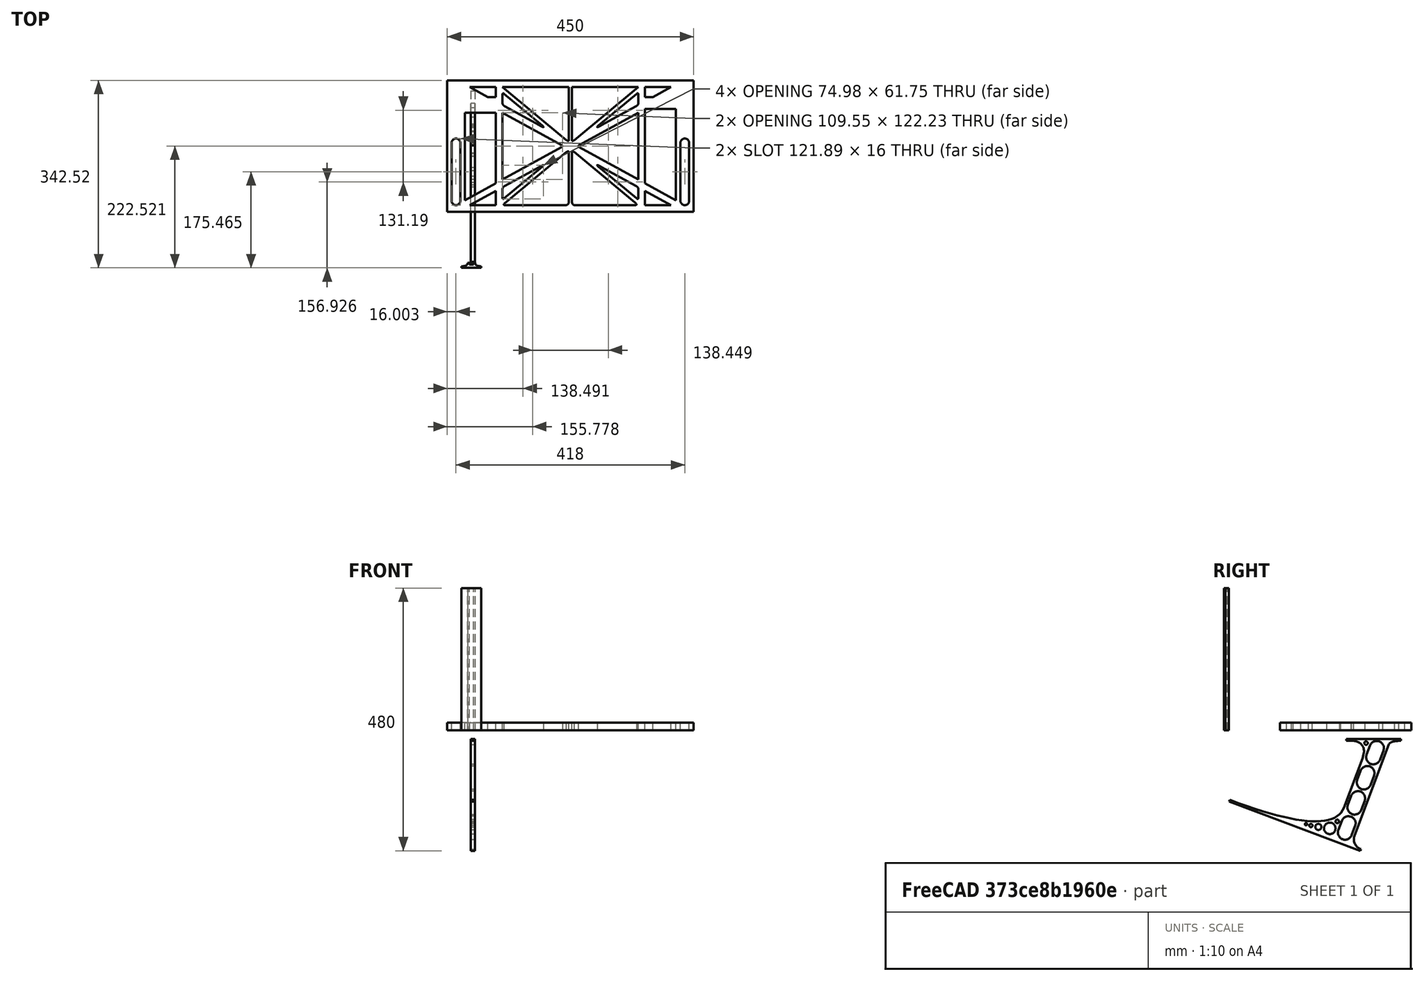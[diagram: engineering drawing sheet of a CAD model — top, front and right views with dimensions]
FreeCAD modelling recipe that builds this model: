
FCSTD DOCUMENT  (FreeCAD 0.19R0.19.2)
Label: laptopStand083
License: All rights reserved
LicenseURL: http://en.wikipedia.org/wiki/All_rights_reserved
objects: Sketcher::SketchObject×3, Part::Extrusion×3
note: 6 computed .brp shape members not serialized (recipe doc carries the construction recipe); baked Part::Feature solids carry a one-line shape summary decoded from their .brp

FEATURE [Sketcher::SketchObject] Sketch
  FullyConstrained = true
  sketch-geometry (202):
    g0: LineSegment StartX=-10.9272 StartY=-82.7794 StartZ=0 EndX=46.0728 EndY=-51.4823 EndZ=0
    g1: LineSegment StartX=366.073 StartY=-91.7794 StartZ=0 EndX=318.073 EndY=-65.424 EndZ=0
    g2: LineSegment StartX=-10.9272 StartY=77.3346 StartZ=0 EndX=-10.9272 EndY=-82.7794 EndZ=0
    g3: LineSegment StartX=375.073 StartY=-82.7794 StartZ=0 EndX=375.073 EndY=83.9235 EndZ=0
    g4: LineSegment StartX=-1.92719 StartY=-91.7794 StartZ=0 EndX=46.0728 EndY=-91.7794 EndZ=0
    g5: LineSegment StartX=318.073 StartY=124.221 StartZ=0 EndX=366.073 EndY=124.221 EndZ=0
    g6: LineSegment StartX=306.073 StartY=124.221 StartZ=0 EndX=189.124 EndY=27.0628 EndZ=0
    g7: LineSegment StartX=175.022 StartY=27.0628 StartZ=0 EndX=58.0728 EndY=124.221 EndZ=0
    g8: LineSegment StartX=306.073 StartY=77.3346 StartZ=0 EndX=306.073 EndY=-44.8935 EndZ=0
    g9: LineSegment StartX=318.073 StartY=83.9235 StartZ=0 EndX=318.073 EndY=-51.4823 EndZ=0
    g10: LineSegment StartX=318.073 StartY=-51.4823 StartZ=0 EndX=375.073 EndY=-82.7794 EndZ=0
    g11: LineSegment StartX=318.073 StartY=-65.424 StartZ=0 EndX=318.073 EndY=-91.7794 EndZ=0
    g12: LineSegment StartX=318.073 StartY=-91.7794 StartZ=0 EndX=366.073 EndY=-91.7794 EndZ=0
    g13: LineSegment StartX=58.0728 StartY=-44.8935 StartZ=0 EndX=58.0728 EndY=77.3346 EndZ=0
    g14: LineSegment StartX=46.0728 StartY=-65.424 StartZ=0 EndX=-1.92719 EndY=-91.7794 EndZ=0
    g15: LineSegment StartX=46.0728 StartY=-65.424 StartZ=0 EndX=46.0728 EndY=-91.7794 EndZ=0
    g16: LineSegment StartX=46.0728 StartY=77.3346 StartZ=0 EndX=46.0728 EndY=-51.4823 EndZ=0
    g17: LineSegment StartX=-42.9272 StartY=136.221 StartZ=0 EndX=-42.9272 EndY=-103.779 EndZ=0
    g18: LineSegment StartX=407.073 StartY=136.221 StartZ=0 EndX=407.073 EndY=-103.779 EndZ=0
    g19: LineSegment StartX=179.022 StartY=27.0628 StartZ=0 EndX=179.022 EndY=124.221 EndZ=0
    g20: LineSegment StartX=185.124 StartY=27.0628 StartZ=0 EndX=185.124 EndY=124.221 EndZ=0
    g21: ArcOfCircle CenterX=-26.9272 CenterY=22.1087 CenterZ=0 NormalX=0 NormalY=0 NormalZ=1 AngleXU=0 Radius=8 StartAngle=1e-16 EndAngle=3.14159
    g22: ArcOfCircle CenterX=-26.9272 CenterY=-83.7794 CenterZ=0 NormalX=0 NormalY=0 NormalZ=1 AngleXU=0 Radius=8 StartAngle=3.14159 EndAngle=6.28319
    g23: LineSegment StartX=-34.9272 StartY=22.1087 StartZ=0 EndX=-34.9272 EndY=-83.7794 EndZ=0
    g24: LineSegment StartX=-18.9272 StartY=22.1087 StartZ=0 EndX=-18.9272 EndY=-83.7794 EndZ=0
    g25: ArcOfCircle CenterX=391.073 CenterY=22.1087 CenterZ=0 NormalX=0 NormalY=0 NormalZ=1 AngleXU=0 Radius=8 StartAngle=-4.4e-15 EndAngle=3.14159
    g26: LineSegment StartX=399.073 StartY=22.1087 StartZ=0 EndX=399.073 EndY=-83.7794 EndZ=0
    g27: LineSegment StartX=383.073 StartY=22.1087 StartZ=0 EndX=383.073 EndY=-83.7794 EndZ=0
    g28: ArcOfCircle CenterX=391.073 CenterY=-83.7794 CenterZ=0 NormalX=0 NormalY=0 NormalZ=1 AngleXU=0 Radius=8 StartAngle=3.14159 EndAngle=6.28319
    g29: Circle CenterX=175.022 CenterY=27.0628 CenterZ=0 NormalX=0 NormalY=0 NormalZ=1 AngleXU=0 Radius=1
    g30: Circle CenterX=179.022 CenterY=24.8665 CenterZ=0 NormalX=0 NormalY=0 NormalZ=1 AngleXU=0 Radius=1
    g31: Circle CenterX=179.022 CenterY=27.0628 CenterZ=0 NormalX=0 NormalY=0 NormalZ=1 AngleXU=0 Radius=1
    g32: BSplineCurve PolesCount=3 KnotsCount=2 Degree=2 IsPeriodic=0
    g33: GeomPoint X=175.022 Y=27.0628 Z=0
    g34: GeomPoint X=179.022 Y=27.0628 Z=0
    g35: Circle CenterX=189.124 CenterY=27.0628 CenterZ=0 NormalX=0 NormalY=0 NormalZ=1 AngleXU=0 Radius=1
    g36: Circle CenterX=185.124 CenterY=24.8665 CenterZ=0 NormalX=0 NormalY=0 NormalZ=1 AngleXU=0 Radius=1
    g37: Circle CenterX=185.124 CenterY=27.0628 CenterZ=0 NormalX=0 NormalY=0 NormalZ=1 AngleXU=0 Radius=1
    g38: BSplineCurve PolesCount=3 KnotsCount=2 Degree=2 IsPeriodic=0
    g39: GeomPoint X=189.124 Y=27.0628 Z=0
    g40: GeomPoint X=185.124 Y=27.0628 Z=0
    g41: Circle CenterX=175.022 CenterY=5.37834 CenterZ=0 NormalX=0 NormalY=0 NormalZ=1 AngleXU=0 Radius=1
    g42: Circle CenterX=179.022 CenterY=7.57463 CenterZ=0 NormalX=0 NormalY=0 NormalZ=1 AngleXU=0 Radius=1
    g43: Circle CenterX=179.022 CenterY=5.34704 CenterZ=0 NormalX=0 NormalY=0 NormalZ=1 AngleXU=0 Radius=1
    g44: BSplineCurve PolesCount=3 KnotsCount=2 Degree=2 IsPeriodic=0
    g45: GeomPoint X=175.022 Y=5.37834 Z=0
    g46: GeomPoint X=179.022 Y=5.34704 Z=0
    g47: Circle CenterX=189.124 CenterY=5.37834 CenterZ=0 NormalX=0 NormalY=0 NormalZ=1 AngleXU=0 Radius=1
    g48: Circle CenterX=185.124 CenterY=7.57463 CenterZ=0 NormalX=0 NormalY=0 NormalZ=1 AngleXU=0 Radius=1
    g49: Circle CenterX=185.124 CenterY=5.34704 CenterZ=0 NormalX=0 NormalY=0 NormalZ=1 AngleXU=0 Radius=1
    g50: BSplineCurve PolesCount=3 KnotsCount=2 Degree=2 IsPeriodic=0
    g51: GeomPoint X=189.124 Y=5.37834 Z=0
    g52: GeomPoint X=185.124 Y=5.34704 Z=0
    g53: Circle CenterX=165.871 CenterY=18.1458 CenterZ=0 NormalX=0 NormalY=0 NormalZ=1 AngleXU=0 Radius=1
    g54: Circle CenterX=169.377 CenterY=16.2206 CenterZ=0 NormalX=0 NormalY=0 NormalZ=1 AngleXU=0 Radius=1
    g55: Circle CenterX=165.871 CenterY=14.2954 CenterZ=0 NormalX=0 NormalY=0 NormalZ=1 AngleXU=0 Radius=1
    g56: BSplineCurve PolesCount=3 KnotsCount=2 Degree=2 IsPeriodic=0
    g57: GeomPoint X=165.871 Y=18.1458 Z=0
    g58: GeomPoint X=165.871 Y=14.2954 Z=0
    g59: Circle CenterX=198.275 CenterY=18.1458 CenterZ=0 NormalX=0 NormalY=0 NormalZ=1 AngleXU=0 Radius=1
    g60: Circle CenterX=194.768 CenterY=16.2206 CenterZ=0 NormalX=0 NormalY=0 NormalZ=1 AngleXU=0 Radius=1
    g61: Circle CenterX=198.275 CenterY=14.2954 CenterZ=0 NormalX=0 NormalY=0 NormalZ=1 AngleXU=0 Radius=1
    g62: BSplineCurve PolesCount=3 KnotsCount=2 Degree=2 IsPeriodic=0
    g63: GeomPoint X=198.275 Y=18.1458 Z=0
    g64: GeomPoint X=198.275 Y=14.2954 Z=0
    g65: LineSegment StartX=165.871 StartY=18.1458 StartZ=0 EndX=58.0728 EndY=77.3346 EndZ=0
    g66: LineSegment StartX=58.0728 StartY=-44.8935 StartZ=0 EndX=165.871 EndY=14.2954 EndZ=0
    g67: LineSegment StartX=198.275 StartY=18.1458 StartZ=0 EndX=306.073 EndY=77.3346 EndZ=0
    g68: LineSegment StartX=198.275 StartY=14.2954 StartZ=0 EndX=306.073 EndY=-44.8935 EndZ=0
    g69: LineSegment StartX=407.073 StartY=-103.779 StartZ=0 EndX=-42.9272 EndY=-103.779 EndZ=0
    g70: LineSegment StartX=407.073 StartY=136.221 StartZ=0 EndX=-42.9272 EndY=136.221 EndZ=0
    g71: LineSegment StartX=46.0728 StartY=77.3346 StartZ=0 EndX=-10.9272 EndY=77.3346 EndZ=0
    g72: LineSegment StartX=46.0728 StartY=105.865 StartZ=0 EndX=31.5028 EndY=105.865 EndZ=0
    g73: LineSegment StartX=46.0728 StartY=124.221 StartZ=0 EndX=46.0728 EndY=105.865 EndZ=0
    g74: LineSegment StartX=-1.92719 StartY=124.221 StartZ=0 EndX=31.5028 EndY=105.865 EndZ=0
    g75: LineSegment StartX=46.0728 StartY=124.221 StartZ=0 EndX=-1.92719 EndY=124.221 EndZ=0
    g76: LineSegment StartX=318.073 StartY=83.9235 StartZ=0 EndX=375.073 EndY=83.9235 EndZ=0
    g77: LineSegment StartX=318.073 StartY=105.865 StartZ=0 EndX=332.643 EndY=105.865 EndZ=0
    g78: LineSegment StartX=332.643 StartY=105.865 StartZ=0 EndX=366.073 EndY=124.221 EndZ=0
    g79: LineSegment StartX=318.073 StartY=124.221 StartZ=0 EndX=318.073 EndY=105.865 EndZ=0
    g80: Circle CenterX=125.607 CenterY=54.1951 CenterZ=0 NormalX=0 NormalY=0 NormalZ=1 AngleXU=0 Radius=1
    g81: Circle CenterX=139.632 CenterY=46.4944 CenterZ=0 NormalX=0 NormalY=0 NormalZ=1 AngleXU=0 Radius=1
    g82: Circle CenterX=127.326 CenterY=56.7187 CenterZ=0 NormalX=0 NormalY=0 NormalZ=1 AngleXU=0 Radius=1
    g83: BSplineCurve PolesCount=3 KnotsCount=2 Degree=2 IsPeriodic=0
    g84: GeomPoint X=125.607 Y=54.1951 Z=0
    g85: GeomPoint X=127.326 Y=56.7187 Z=0
    g86: Circle CenterX=236.821 CenterY=56.7187 CenterZ=0 NormalX=0 NormalY=0 NormalZ=1 AngleXU=0 Radius=1
    g87: Circle CenterX=224.513 CenterY=46.4944 CenterZ=0 NormalX=0 NormalY=0 NormalZ=1 AngleXU=0 Radius=1
    g88: Circle CenterX=238.538 CenterY=54.1951 CenterZ=0 NormalX=0 NormalY=0 NormalZ=1 AngleXU=0 Radius=1
    g89: BSplineCurve PolesCount=3 KnotsCount=2 Degree=2 IsPeriodic=0
    g90: GeomPoint X=236.821 Y=56.7187 Z=0
    g91: GeomPoint X=238.538 Y=54.1951 Z=0
    g92: Circle CenterX=238.538 CenterY=-21.7539 CenterZ=0 NormalX=0 NormalY=0 NormalZ=1 AngleXU=0 Radius=1
    g93: Circle CenterX=224.513 CenterY=-14.0532 CenterZ=0 NormalX=0 NormalY=0 NormalZ=1 AngleXU=0 Radius=1
    g94: Circle CenterX=236.821 CenterY=-24.2775 CenterZ=0 NormalX=0 NormalY=0 NormalZ=1 AngleXU=0 Radius=1
    g95: BSplineCurve PolesCount=3 KnotsCount=2 Degree=2 IsPeriodic=0
    g96: GeomPoint X=238.538 Y=-21.7539 Z=0
    g97: GeomPoint X=236.821 Y=-24.2775 Z=0
    g98: Circle CenterX=125.607 CenterY=-21.7539 CenterZ=0 NormalX=0 NormalY=0 NormalZ=1 AngleXU=0 Radius=1
    g99: Circle CenterX=139.632 CenterY=-14.0532 CenterZ=0 NormalX=0 NormalY=0 NormalZ=1 AngleXU=0 Radius=1
    g100: Circle CenterX=127.325 CenterY=-24.2775 CenterZ=0 NormalX=0 NormalY=0 NormalZ=1 AngleXU=0 Radius=1
    g101: BSplineCurve PolesCount=3 KnotsCount=2 Degree=2 IsPeriodic=0
    g102: GeomPoint X=125.607 Y=-21.7539 Z=0
    g103: GeomPoint X=127.325 Y=-24.2775 Z=0
    g104: Circle CenterX=302.996 CenterY=111.695 CenterZ=0 NormalX=0 NormalY=0 NormalZ=1 AngleXU=0 Radius=1
    g105: Circle CenterX=306.073 CenterY=114.251 CenterZ=0 NormalX=0 NormalY=0 NormalZ=1 AngleXU=0 Radius=1
    g106: Circle CenterX=306.073 CenterY=110.251 CenterZ=0 NormalX=0 NormalY=0 NormalZ=1 AngleXU=0 Radius=1
    g107: BSplineCurve PolesCount=3 KnotsCount=2 Degree=2 IsPeriodic=0
    g108: GeomPoint X=302.996 Y=111.695 Z=0
    g109: GeomPoint X=306.073 Y=110.251 Z=0
    g110: Circle CenterX=306.073 CenterY=95.2763 CenterZ=0 NormalX=0 NormalY=0 NormalZ=1 AngleXU=0 Radius=1
    g111: Circle CenterX=306.073 CenterY=91.2763 CenterZ=0 NormalX=0 NormalY=0 NormalZ=1 AngleXU=0 Radius=1
    g112: Circle CenterX=302.567 CenterY=89.3511 CenterZ=0 NormalX=0 NormalY=0 NormalZ=1 AngleXU=0 Radius=1
    g113: BSplineCurve PolesCount=3 KnotsCount=2 Degree=2 IsPeriodic=0
    g114: GeomPoint X=306.073 Y=95.2763 Z=0
    g115: GeomPoint X=302.567 Y=89.3511 Z=0
    g116: LineSegment StartX=306.073 StartY=110.251 StartZ=0 EndX=306.073 EndY=95.2763 EndZ=0
    g117: LineSegment StartX=302.996 StartY=111.695 StartZ=0 EndX=236.821 EndY=56.7187 EndZ=0
    g118: LineSegment StartX=238.538 StartY=54.1951 StartZ=0 EndX=302.567 EndY=89.3511 EndZ=0
    g119: Circle CenterX=61.1496 CenterY=111.695 CenterZ=0 NormalX=0 NormalY=0 NormalZ=1 AngleXU=0 Radius=1
    g120: Circle CenterX=58.0728 CenterY=114.251 CenterZ=0 NormalX=0 NormalY=0 NormalZ=1 AngleXU=0 Radius=1
    g121: Circle CenterX=58.0728 CenterY=110.251 CenterZ=0 NormalX=0 NormalY=0 NormalZ=1 AngleXU=0 Radius=1
    g122: BSplineCurve PolesCount=3 KnotsCount=2 Degree=2 IsPeriodic=0
    g123: GeomPoint X=61.1496 Y=111.695 Z=0
    g124: GeomPoint X=58.0728 Y=110.251 Z=0
    g125: Circle CenterX=61.5791 CenterY=89.3511 CenterZ=0 NormalX=0 NormalY=0 NormalZ=1 AngleXU=0 Radius=1
    g126: Circle CenterX=58.0728 CenterY=91.2763 CenterZ=0 NormalX=0 NormalY=0 NormalZ=1 AngleXU=0 Radius=1
    g127: Circle CenterX=58.0728 CenterY=95.2763 CenterZ=0 NormalX=0 NormalY=0 NormalZ=1 AngleXU=0 Radius=1
    g128: BSplineCurve PolesCount=3 KnotsCount=2 Degree=2 IsPeriodic=0
    g129: GeomPoint X=61.5791 Y=89.3511 Z=0
    g130: GeomPoint X=58.0728 Y=95.2763 Z=0
    g131: LineSegment StartX=58.0728 StartY=110.251 StartZ=0 EndX=58.0728 EndY=95.2763 EndZ=0
    g132: LineSegment StartX=61.1496 StartY=111.695 StartZ=0 EndX=127.326 EndY=56.7187 EndZ=0
    g133: LineSegment StartX=125.607 StartY=54.1951 StartZ=0 EndX=61.5791 EndY=89.3511 EndZ=0
    g134: Circle CenterX=61.5791 CenterY=-56.9099 CenterZ=0 NormalX=0 NormalY=0 NormalZ=1 AngleXU=0 Radius=1
    g135: Circle CenterX=58.0728 CenterY=-58.8351 CenterZ=0 NormalX=0 NormalY=0 NormalZ=1 AngleXU=0 Radius=1
    g136: Circle CenterX=58.0728 CenterY=-62.8351 CenterZ=0 NormalX=0 NormalY=0 NormalZ=1 AngleXU=0 Radius=1
    g137: BSplineCurve PolesCount=3 KnotsCount=2 Degree=2 IsPeriodic=0
    g138: GeomPoint X=61.5791 Y=-56.9099 Z=0
    g139: GeomPoint X=58.0728 Y=-62.8351 Z=0
    g140: Circle CenterX=58.0728 CenterY=-77.8102 CenterZ=0 NormalX=0 NormalY=0 NormalZ=1 AngleXU=0 Radius=1
    g141: Circle CenterX=58.0728 CenterY=-81.8102 CenterZ=0 NormalX=0 NormalY=0 NormalZ=1 AngleXU=0 Radius=1
    g142: Circle CenterX=61.1496 CenterY=-79.2541 CenterZ=0 NormalX=0 NormalY=0 NormalZ=1 AngleXU=0 Radius=1
    g143: BSplineCurve PolesCount=3 KnotsCount=2 Degree=2 IsPeriodic=0
    g144: GeomPoint X=58.0728 Y=-77.8102 Z=0
    g145: GeomPoint X=61.1496 Y=-79.2541 Z=0
    g146: LineSegment StartX=58.0728 StartY=-62.8351 StartZ=0 EndX=58.0728 EndY=-77.8102 EndZ=0
    g147: LineSegment StartX=61.1496 StartY=-79.2541 StartZ=0 EndX=127.325 EndY=-24.2775 EndZ=0
    g148: LineSegment StartX=125.607 StartY=-21.7539 StartZ=0 EndX=61.5791 EndY=-56.9099 EndZ=0
    g149: Circle CenterX=302.567 CenterY=-56.9099 CenterZ=0 NormalX=0 NormalY=0 NormalZ=1 AngleXU=0 Radius=1
    g150: Circle CenterX=306.073 CenterY=-58.8351 CenterZ=0 NormalX=0 NormalY=0 NormalZ=1 AngleXU=0 Radius=1
    g151: Circle CenterX=306.073 CenterY=-62.8351 CenterZ=0 NormalX=0 NormalY=0 NormalZ=1 AngleXU=0 Radius=1
    g152: BSplineCurve PolesCount=3 KnotsCount=2 Degree=2 IsPeriodic=0
    g153: GeomPoint X=302.567 Y=-56.9099 Z=0
    g154: GeomPoint X=306.073 Y=-62.8351 Z=0
    g155: Circle CenterX=302.996 CenterY=-79.2541 CenterZ=0 NormalX=0 NormalY=0 NormalZ=1 AngleXU=0 Radius=1
    g156: Circle CenterX=306.073 CenterY=-81.8102 CenterZ=0 NormalX=0 NormalY=0 NormalZ=1 AngleXU=0 Radius=1
    g157: Circle CenterX=306.073 CenterY=-77.8102 CenterZ=0 NormalX=0 NormalY=0 NormalZ=1 AngleXU=0 Radius=1
    g158: BSplineCurve PolesCount=3 KnotsCount=2 Degree=2 IsPeriodic=0
    g159: GeomPoint X=302.996 Y=-79.2541 Z=0
    g160: GeomPoint X=306.073 Y=-77.8102 Z=0
    g161: LineSegment StartX=306.073 StartY=-62.8351 StartZ=0 EndX=306.073 EndY=-77.8102 EndZ=0
    g162: LineSegment StartX=302.996 StartY=-79.2541 StartZ=0 EndX=236.821 EndY=-24.2775 EndZ=0
    g163: LineSegment StartX=238.538 StartY=-21.7539 StartZ=0 EndX=302.567 EndY=-56.9099 EndZ=0
    g164: Circle CenterX=61.6457 CenterY=-88.8112 CenterZ=0 NormalX=0 NormalY=0 NormalZ=1 AngleXU=0 Radius=1
    g165: Circle CenterX=58.0728 CenterY=-91.7794 CenterZ=0 NormalX=0 NormalY=0 NormalZ=1 AngleXU=0 Radius=1
    g166: Circle CenterX=63.9135 CenterY=-91.7794 CenterZ=0 NormalX=0 NormalY=0 NormalZ=1 AngleXU=0 Radius=1
    g167: BSplineCurve PolesCount=3 KnotsCount=2 Degree=2 IsPeriodic=0
    g168: GeomPoint X=61.6457 Y=-88.8112 Z=0
    g169: GeomPoint X=63.9135 Y=-91.7794 Z=0
    g170: Circle CenterX=179.022 CenterY=-85.8163 CenterZ=0 NormalX=0 NormalY=0 NormalZ=1 AngleXU=0 Radius=1
    g171: Circle CenterX=179.022 CenterY=-91.7794 CenterZ=0 NormalX=0 NormalY=0 NormalZ=1 AngleXU=0 Radius=1
    g172: Circle CenterX=171.895 CenterY=-91.7794 CenterZ=0 NormalX=0 NormalY=0 NormalZ=1 AngleXU=0 Radius=1
    g173: BSplineCurve PolesCount=3 KnotsCount=2 Degree=2 IsPeriodic=0
    g174: GeomPoint X=179.022 Y=-85.8163 Z=0
    g175: GeomPoint X=171.895 Y=-91.7794 Z=0
    g176: Circle CenterX=185.124 CenterY=-86.2028 CenterZ=0 NormalX=0 NormalY=0 NormalZ=1 AngleXU=0 Radius=1
    g177: Circle CenterX=185.124 CenterY=-91.7794 CenterZ=0 NormalX=0 NormalY=0 NormalZ=1 AngleXU=0 Radius=1
    g178: Circle CenterX=191.747 CenterY=-91.7794 CenterZ=0 NormalX=0 NormalY=0 NormalZ=1 AngleXU=0 Radius=1
    g179: BSplineCurve PolesCount=3 KnotsCount=2 Degree=2 IsPeriodic=0
    g180: GeomPoint X=185.124 Y=-86.2028 Z=0
    g181: GeomPoint X=191.747 Y=-91.7794 Z=0
    g182: Circle CenterX=299.888 CenterY=-86.6413 CenterZ=0 NormalX=0 NormalY=0 NormalZ=1 AngleXU=0 Radius=1
    g183: Circle CenterX=306.073 CenterY=-91.7794 CenterZ=0 NormalX=0 NormalY=0 NormalZ=1 AngleXU=0 Radius=1
    g184: Circle CenterX=298.776 CenterY=-91.7794 CenterZ=0 NormalX=0 NormalY=0 NormalZ=1 AngleXU=0 Radius=1
    g185: BSplineCurve PolesCount=3 KnotsCount=2 Degree=2 IsPeriodic=0
    g186: GeomPoint X=299.888 Y=-86.6413 Z=0
    g187: GeomPoint X=298.776 Y=-91.7794 Z=0
    g188: LineSegment StartX=189.124 StartY=5.37834 StartZ=0 EndX=299.888 EndY=-86.6413 EndZ=0
    g189: LineSegment StartX=298.776 StartY=-91.7794 StartZ=0 EndX=191.747 EndY=-91.7794 EndZ=0
    g190: LineSegment StartX=185.124 StartY=-86.2028 StartZ=0 EndX=185.124 EndY=5.34704 EndZ=0
    g191: LineSegment StartX=179.022 StartY=5.34704 StartZ=0 EndX=179.022 EndY=-85.8163 EndZ=0
    g192: LineSegment StartX=171.895 StartY=-91.7794 StartZ=0 EndX=63.9135 EndY=-91.7794 EndZ=0
    g193: LineSegment StartX=61.6457 StartY=-88.8112 StartZ=0 EndX=175.022 EndY=5.37834 EndZ=0
    g194: LineSegment StartX=306.073 StartY=124.221 StartZ=0 EndX=302.996 EndY=121.665 EndZ=0
    g195: LineSegment StartX=306.073 StartY=124.221 StartZ=0 EndX=302.073 EndY=124.221 EndZ=0
    g196: LineSegment StartX=185.124 StartY=124.221 StartZ=0 EndX=189.124 EndY=124.221 EndZ=0
    g197: LineSegment StartX=185.124 StartY=124.221 StartZ=0 EndX=185.124 EndY=120.221 EndZ=0
    g198: LineSegment StartX=179.022 StartY=124.221 StartZ=0 EndX=179.022 EndY=120.221 EndZ=0
    g199: LineSegment StartX=179.022 StartY=124.221 StartZ=0 EndX=175.022 EndY=124.221 EndZ=0
    g200: LineSegment StartX=58.0728 StartY=124.221 StartZ=0 EndX=62.0728 EndY=124.221 EndZ=0
    g201: LineSegment StartX=58.0728 StartY=124.221 StartZ=0 EndX=61.1496 EndY=121.665 EndZ=0
  constraints (357):
    c: Horizontal(g4)
    c: Horizontal(g5)
    c: Coincident(g9,g10)
    c: Coincident(g11,g1)
    c: Tangent(g9,g11)
    c: Coincident(g15,g14)
    c: Coincident(g0,g16)
    c: Block(g7)
    c: Block(g6)
    c: Block(g10)
    c: Block(g3)
    c: Block(g1)
    c: Block(g11)
    c: Block(g15)
    c: Block(g14)
    c: Block(g0)
    c: Block(g2)
    c: Block(g8)
    c: Block(g5)
    c: Block(g12)
    c: Block(g4)
    c: Vertical(g17)
    c: Vertical(g18)
    c: Block(g18)
    c: Block(g17)
    c: Vertical(g19)
    c: Vertical(g20)
    c: Block(g19)
    c: Block(g20)
    c: Tangent(g21,g24) = 1.5708
    c: Tangent(g21,g23) = -1.5708
    c: Tangent(g23,g22) = -1.5708
    c: Tangent(g24,g22) = 1.5708
    c: Vertical(g23)
    c: Equal(g21,g22)
    c: Block(g24)
    c: Block(g23)
    c: Tangent(g25,g26) = 1.5708
    c: Tangent(g26,g28) = 1.5708
    c: Equal(g25,g28)
    c: Coincident(g27,g25)
    c: Coincident(g27,g28)
    c: Block(g26)
    c: Block(g27)
    c: Coincident(g32,g7)
    c: Weight(g29) = 1
    c: Equal(g29,g30)
    c: Equal(g29,g31)
    c: Coincident(g32,g19)
    c: InternalAlignment(g29,g32)
    c: InternalAlignment(g30,g32)
    c: InternalAlignment(g31,g32)
    c: InternalAlignment(g33,g32)
    c: InternalAlignment(g34,g32)
    c: Coincident(g38,g6)
    c: Weight(g35) = 1
    c: Equal(g35,g36)
    c: Equal(g35,g37)
    c: Coincident(g38,g20)
    c: InternalAlignment(g35,g38)
    c: InternalAlignment(g36,g38)
    c: InternalAlignment(g37,g38)
    c: InternalAlignment(g39,g38)
    c: InternalAlignment(g40,g38)
    c: Block(g38)
    c: Block(g32)
    c: Weight(g41) = 1
    c: Equal(g41,g42)
    c: Equal(g41,g43)
    c: InternalAlignment(g41,g44)
    c: InternalAlignment(g42,g44)
    c: InternalAlignment(g43,g44)
    c: InternalAlignment(g45,g44)
    c: InternalAlignment(g46,g44)
    c: Weight(g47) = 1
    c: Equal(g47,g48)
    c: Equal(g47,g49)
    c: InternalAlignment(g47,g50)
    c: InternalAlignment(g48,g50)
    c: InternalAlignment(g49,g50)
    c: InternalAlignment(g51,g50)
    c: InternalAlignment(g52,g50)
    c: Block(g50)
    c: Block(g44)
    c: Weight(g53) = 1
    c: Equal(g53,g54)
    c: Equal(g53,g55)
    c: InternalAlignment(g53,g56)
    c: InternalAlignment(g54,g56)
    c: InternalAlignment(g55,g56)
    c: InternalAlignment(g57,g56)
    c: InternalAlignment(g58,g56)
    c: Weight(g59) = 1
    c: Equal(g59,g60)
    c: Equal(g59,g61)
    c: InternalAlignment(g59,g62)
    c: InternalAlignment(g60,g62)
    c: InternalAlignment(g61,g62)
    c: InternalAlignment(g63,g62)
    c: InternalAlignment(g64,g62)
    c: Block(g56)
    c: Block(g62)
    c: Coincident(g65,g56)
    c: Coincident(g65,g13)
    c: Coincident(g66,g13)
    c: Coincident(g66,g56)
    c: Coincident(g67,g62)
    c: Coincident(g67,g8)
    c: Coincident(g68,g62)
    c: Coincident(g68,g8)
    c: Block(g13)
    c: Coincident(g69,g18)
    c: Coincident(g69,g17)
    c: Horizontal(g69)
    c: Distance(g69) = 450
    c: Coincident(g70,g18)
    c: Coincident(g70,g17)
    c: Horizontal(g70)
    c: Horizontal(g71)
    c: Coincident(g16,g71)
    c: Horizontal(g72)
    c: Vertical(g73)
    c: Block(g73)
    c: Block(g72)
    c: Block(g71)
    c: Distance(g73) = 18.3554
    c: Coincident(g75,g73)
    c: Coincident(g75,g74)
    c: Horizontal(g75)
    c: Block(g75)
    c: Block(g74)
    c: Coincident(g72,g74)
    c: Coincident(g2,g71)
    c: Coincident(g76,g9)
    c: Horizontal(g76)
    c: Horizontal(g77)
    c: Block(g76)
    c: Coincident(g78,g5)
    c: Coincident(g79,g5)
    c: Coincident(g79,g77)
    c: Vertical(g79)
    c: Block(g79)
    c: Coincident(g77,g78)
    c: Block(g78)
    c: Coincident(g3,g76)
    c: Weight(g80) = 1
    c: Equal(g80,g81)
    c: Equal(g80,g82)
    c: InternalAlignment(g80,g83)
    c: InternalAlignment(g81,g83)
    c: InternalAlignment(g82,g83)
    c: InternalAlignment(g84,g83)
    c: InternalAlignment(g85,g83)
    c: Block(g83)
    c: Weight(g86) = 1
    c: Equal(g86,g87)
    c: Equal(g86,g88)
    c: InternalAlignment(g86,g89)
    c: InternalAlignment(g87,g89)
    c: InternalAlignment(g88,g89)
    c: InternalAlignment(g90,g89)
    c: InternalAlignment(g91,g89)
    c: Block(g89)
    c: Weight(g92) = 1
    c: Equal(g92,g93)
    c: Equal(g92,g94)
    c: InternalAlignment(g92,g95)
    c: InternalAlignment(g93,g95)
    c: InternalAlignment(g94,g95)
    c: InternalAlignment(g96,g95)
    c: InternalAlignment(g97,g95)
    c: Block(g95)
    c: Weight(g98) = 1
    c: Equal(g98,g99)
    c: Equal(g98,g100)
    c: InternalAlignment(g98,g101)
    c: InternalAlignment(g99,g101)
    c: InternalAlignment(g100,g101)
    c: InternalAlignment(g102,g101)
    c: InternalAlignment(g103,g101)
    c: Block(g101)
    c: Weight(g104) = 1
    c: Equal(g104,g105)
    c: Equal(g104,g106)
    c: InternalAlignment(g104,g107)
    c: InternalAlignment(g105,g107)
    c: InternalAlignment(g106,g107)
    c: InternalAlignment(g108,g107)
    c: InternalAlignment(g109,g107)
    c: Weight(g110) = 1
    c: Equal(g110,g111)
    c: Equal(g110,g112)
    c: InternalAlignment(g110,g113)
    c: InternalAlignment(g111,g113)
    c: InternalAlignment(g112,g113)
    c: InternalAlignment(g114,g113)
    c: InternalAlignment(g115,g113)
    c: Block(g107)
    c: Block(g113)
    c: Coincident(g116,g107)
    c: Coincident(g116,g113)
    c: Vertical(g116)
    c: Coincident(g117,g107)
    c: Coincident(g117,g89)
    c: Coincident(g118,g89)
    c: Coincident(g118,g113)
    c: Weight(g119) = 1
    c: Equal(g119,g120)
    c: Equal(g119,g121)
    c: InternalAlignment(g119,g122)
    c: InternalAlignment(g120,g122)
    c: InternalAlignment(g121,g122)
    c: InternalAlignment(g123,g122)
    c: InternalAlignment(g124,g122)
    c: Weight(g125) = 1
    c: Equal(g125,g126)
    c: Equal(g125,g127)
    c: InternalAlignment(g125,g128)
    c: InternalAlignment(g126,g128)
    c: InternalAlignment(g127,g128)
    c: InternalAlignment(g129,g128)
    c: InternalAlignment(g130,g128)
    c: Block(g122)
    c: Block(g128)
    c: Coincident(g131,g122)
    c: Coincident(g131,g128)
    c: Vertical(g131)
    c: Coincident(g132,g122)
    c: Coincident(g132,g83)
    c: Coincident(g133,g83)
    c: Coincident(g133,g128)
    c: Weight(g134) = 1
    c: Equal(g134,g135)
    c: Equal(g134,g136)
    c: InternalAlignment(g134,g137)
    c: InternalAlignment(g135,g137)
    c: InternalAlignment(g136,g137)
    c: InternalAlignment(g138,g137)
    c: InternalAlignment(g139,g137)
    c: Weight(g140) = 1
    c: Equal(g140,g141)
    c: Equal(g140,g142)
    c: InternalAlignment(g140,g143)
    c: InternalAlignment(g141,g143)
    c: InternalAlignment(g142,g143)
    c: InternalAlignment(g144,g143)
    c: InternalAlignment(g145,g143)
    c: Block(g137)
    c: Block(g143)
    c: Coincident(g146,g137)
    c: Coincident(g146,g143)
    c: Vertical(g146)
    c: Coincident(g147,g143)
    c: Coincident(g147,g101)
    c: Coincident(g148,g101)
    c: Coincident(g148,g137)
    c: Weight(g149) = 1
    c: Equal(g149,g150)
    c: Equal(g149,g151)
    c: InternalAlignment(g149,g152)
    c: InternalAlignment(g150,g152)
    c: InternalAlignment(g151,g152)
    c: InternalAlignment(g153,g152)
    c: InternalAlignment(g154,g152)
    c: Weight(g155) = 1
    c: Equal(g155,g156)
    c: Equal(g155,g157)
    c: InternalAlignment(g155,g158)
    c: InternalAlignment(g156,g158)
    c: InternalAlignment(g157,g158)
    c: InternalAlignment(g159,g158)
    c: InternalAlignment(g160,g158)
    c: Block(g152)
    c: Block(g158)
    c: Coincident(g161,g152)
    c: Coincident(g161,g158)
    c: Vertical(g161)
    c: Coincident(g162,g158)
    c: Coincident(g162,g95)
    c: Coincident(g163,g95)
    c: Coincident(g163,g152)
    c: Weight(g164) = 1
    c: Equal(g164,g165)
    c: Equal(g164,g166)
    c: InternalAlignment(g164,g167)
    c: InternalAlignment(g165,g167)
    c: InternalAlignment(g166,g167)
    c: InternalAlignment(g168,g167)
    c: InternalAlignment(g169,g167)
    c: Weight(g170) = 1
    c: Equal(g170,g171)
    c: Equal(g170,g172)
    c: InternalAlignment(g170,g173)
    c: InternalAlignment(g171,g173)
    c: InternalAlignment(g172,g173)
    c: InternalAlignment(g174,g173)
    c: InternalAlignment(g175,g173)
    c: Weight(g176) = 1
    c: Equal(g176,g177)
    c: Equal(g176,g178)
    c: InternalAlignment(g176,g179)
    c: InternalAlignment(g177,g179)
    c: InternalAlignment(g178,g179)
    c: InternalAlignment(g180,g179)
    c: InternalAlignment(g181,g179)
    c: Weight(g182) = 1
    c: Equal(g182,g183)
    c: Equal(g182,g184)
    c: InternalAlignment(g182,g185)
    c: InternalAlignment(g183,g185)
    c: InternalAlignment(g184,g185)
    c: InternalAlignment(g186,g185)
    c: InternalAlignment(g187,g185)
    c: Block(g185)
    c: Block(g179)
    c: Block(g173)
    c: Block(g167)
    c: Coincident(g188,g50)
    c: Coincident(g188,g185)
    c: Coincident(g189,g185)
    c: Coincident(g189,g179)
    c: Horizontal(g189)
    c: Coincident(g190,g179)
    c: Coincident(g190,g50)
    c: Vertical(g190)
    c: Coincident(g191,g44)
    c: Coincident(g191,g173)
    c: Vertical(g191)
    c: Coincident(g192,g173)
    c: Coincident(g192,g167)
    c: Horizontal(g192)
    c: Coincident(g193,g167)
    c: Coincident(g193,g44)
    c: Horizontal(g195)
    c: Horizontal(g196)
    c: Vertical(g197)
    c: Vertical(g198)
    c: Horizontal(g199)
    c: Horizontal(g200)
    c: Parallel(g201,g7)
    c: Parallel(g194,g6)
    c: Distance(g194) = 4
    c: Distance(g195) = 4
    c: Distance(g196) = 4
    c: Distance(g197) = 4
    c: Distance(g198) = 4
    c: Distance(g199) = 4
    c: Distance(g200) = 4
    c: Distance(g201) = 4
    c: Coincident(g200,g7)
    c: Coincident(g201,g7)
    c: Coincident(g198,g19)
    c: Coincident(g199,g19)
    c: Coincident(g197,g20)
    c: Coincident(g196,g20)
    c: Coincident(g194,g6)
    c: Coincident(g195,g6)
FEATURE [Sketcher::SketchObject] Sketch001
  FullyConstrained = true
  MapMode = 4
  Placement = pos=(0,0,0) rot=(0.57735,0.57735,0.57735;2.0944rad)
  Support = -> [Sketch]
  sketch-geometry (46):
    g0: BSplineCurve PolesCount=3 KnotsCount=2 Degree=2 IsPeriodic=0
    g1: ArcOfCircle CenterX=73.1223 CenterY=-32.291 CenterZ=0 NormalX=0 NormalY=0 NormalZ=1 AngleXU=0 Radius=13 StartAngle=5.92268 EndAngle=9.06428
    g2: ArcOfCircle CenterX=66.7816 CenterY=-49.1439 CenterZ=0 NormalX=0 NormalY=0 NormalZ=1 AngleXU=0 Radius=13 StartAngle=2.78068 EndAngle=5.92131
    g3: ArcOfCircle CenterX=55.9263 CenterY=-78.1807 CenterZ=0 NormalX=0 NormalY=0 NormalZ=1 AngleXU=0 Radius=13 StartAngle=5.92268 EndAngle=9.06428
    g4: ArcOfCircle CenterX=49.5884 CenterY=-95.0342 CenterZ=0 NormalX=0 NormalY=0 NormalZ=1 AngleXU=0 Radius=13 StartAngle=2.78068 EndAngle=5.92131
    g5: ArcOfCircle CenterX=38.7206 CenterY=-124.067 CenterZ=0 NormalX=0 NormalY=0 NormalZ=1 AngleXU=0 Radius=13 StartAngle=5.92268 EndAngle=9.06428
    g6: ArcOfCircle CenterX=32.3875 CenterY=-140.92 CenterZ=0 NormalX=0 NormalY=0 NormalZ=1 AngleXU=0 Radius=13 StartAngle=2.78068 EndAngle=5.92131
    g7: ArcOfCircle CenterX=21.4715 CenterY=-169.934 CenterZ=0 NormalX=0 NormalY=0 NormalZ=1 AngleXU=0 Radius=13 StartAngle=5.92268 EndAngle=9.06428
    g8: ArcOfCircle CenterX=15.1336 CenterY=-186.787 CenterZ=0 NormalX=0 NormalY=0 NormalZ=1 AngleXU=0 Radius=13 StartAngle=2.78068 EndAngle=5.92131
    g9-g12: Circle x4 (B-spline internal-alignment scaffolding for g13; pole/knot coordinates omitted)
    g13: BSplineCurve PolesCount=4 KnotsCount=2 Degree=3 IsPeriodic=0
    g14: GeomPoint X=28.8094 Y=-19.0875 Z=0
    g15: GeomPoint X=47.0443 Y=-50.4712 Z=0
    g16: Circle CenterX=53.5586 CenterY=-23.2695 CenterZ=0 NormalX=0 NormalY=0 NormalZ=1 AngleXU=0 Radius=3.24518
    g17: Circle CenterX=-195.441 CenterY=-127.082 CenterZ=0 NormalX=0 NormalY=0 NormalZ=1 AngleXU=0 Radius=1
    g18: Circle CenterX=-8.24091 CenterY=-197.481 CenterZ=0 NormalX=0 NormalY=0 NormalZ=1 AngleXU=0 Radius=1
    g19: Circle CenterX=12.8789 CenterY=-141.321 CenterZ=0 NormalX=0 NormalY=0 NormalZ=1 AngleXU=0 Radius=1
    g20: BSplineCurve PolesCount=3 KnotsCount=2 Degree=2 IsPeriodic=0
    g21: GeomPoint X=-195.441 Y=-127.082 Z=0
    g22: GeomPoint X=12.8789 Y=-141.321 Z=0
    g23: Circle CenterX=-12.8016 CenterY=-179.036 CenterZ=0 NormalX=0 NormalY=0 NormalZ=1 AngleXU=0 Radius=10.5072
    g24: Circle CenterX=0.933922 CenterY=-166.43 CenterZ=0 NormalX=0 NormalY=0 NormalZ=1 AngleXU=0 Radius=3.26661
    g25: Circle CenterX=-33.5518 CenterY=-176.44 CenterZ=0 NormalX=0 NormalY=0 NormalZ=1 AngleXU=0 Radius=5.64388
    g26: Circle CenterX=-47.2366 CenterY=-173.859 CenterZ=0 NormalX=0 NormalY=0 NormalZ=1 AngleXU=0 Radius=3.01653
    g27: Circle CenterX=-56.2595 CenterY=-171.456 CenterZ=0 NormalX=0 NormalY=0 NormalZ=1 AngleXU=0 Radius=2.12826
    g28: ArcOfCircle CenterX=51.2151 CenterY=-198.473 CenterZ=0 NormalX=0 NormalY=0 NormalZ=1 AngleXU=0 Radius=20 StartAngle=2.78189 EndAngle=4.35269
    g29: LineSegment StartX=32.4951 StartY=-191.433 StartZ=0 EndX=94.6578 EndY=-26.1352 EndZ=0
    g30: LineSegment StartX=43.1192 StartY=-220.001 StartZ=0 EndX=-196.497 EndY=-129.89 EndZ=0
    g31: LineSegment StartX=43.1192 StartY=-220.001 StartZ=0 EndX=44.1752 EndY=-217.193 EndZ=0
    g32: LineSegment StartX=117.223 StartY=-19.0875 StartZ=0 EndX=117.223 EndY=-16.0875 EndZ=0
    g33: LineSegment StartX=117.223 StartY=-16.0875 StartZ=0 EndX=17.2232 EndY=-16.0875 EndZ=0
    g34: LineSegment StartX=17.2232 StartY=-16.0875 StartZ=0 EndX=17.2232 EndY=-19.0875 EndZ=0
    g35: LineSegment StartX=28.8094 StartY=-19.0875 StartZ=0 EndX=17.2232 EndY=-19.0875 EndZ=0
    g36: LineSegment StartX=47.0443 StartY=-50.4712 StartZ=0 EndX=12.8789 EndY=-141.321 EndZ=0
    g37: LineSegment StartX=-195.441 StartY=-127.082 StartZ=0 EndX=-196.497 EndY=-129.89 EndZ=0
    g38: LineSegment StartX=85.2866 StartY=-36.8766 StartZ=0 EndX=78.9396 EndY=-53.7463 EndZ=0
    g39: LineSegment StartX=60.9579 StartY=-27.7053 StartZ=0 EndX=54.6191 EndY=-44.5532 EndZ=0
    g40: LineSegment StartX=68.0907 StartY=-82.7664 StartZ=0 EndX=61.7465 EndY=-99.6365 EndZ=0
    g41: LineSegment StartX=43.7619 StartY=-73.595 StartZ=0 EndX=37.426 EndY=-90.4435 EndZ=0
    g42: LineSegment StartX=50.885 StartY=-128.652 StartZ=0 EndX=44.5456 EndY=-145.522 EndZ=0
    g43: LineSegment StartX=26.5562 StartY=-119.481 StartZ=0 EndX=20.2251 EndY=-136.329 EndZ=0
    g44: LineSegment StartX=9.3071 StartY=-165.349 StartZ=0 EndX=2.97115 EndY=-182.197 EndZ=0
    g45: LineSegment StartX=33.6358 StartY=-174.52 StartZ=0 EndX=27.2917 EndY=-191.39 EndZ=0
  constraints (71):
    c: Block(g0)
    c: Block(g1)
    c: Block(g2)
    c: Block(g4)
    c: Block(g3)
    c: Block(g6)
    c: Block(g5)
    c: Block(g8)
    c: Block(g7)
    c: Weight(g9) = 1
    c: Equal(g9,g10)
    c: Equal(g9,g11)
    c: Equal(g9,g12)
    c: InternalAlignment(g9-g12 -> g13) x4
    c: InternalAlignment(g14,g13)
    c: InternalAlignment(g15,g13)
    c: Block(g16)
    c: Weight(g17) = 1
    c: Equal(g17,g18)
    c: Equal(g17,g19)
    c: InternalAlignment(g17,g20)
    c: InternalAlignment(g18,g20)
    c: InternalAlignment(g19,g20)
    c: InternalAlignment(g21,g20)
    c: InternalAlignment(g22,g20)
    c: Block(g20)
    c: Block(g23)
    c: Block(g24)
    c: Block(g25)
    c: Block(g26)
    c: Block(g27)
    c: Block(g28)
    c: Coincident(g29,g28)
    c: Coincident(g29,g0)
    c: Block(g13)
    c: Coincident(g31,g30)
    c: Coincident(g31,g28)
    c: Block(g31)
    c: Coincident(g32,g0)
    c: Vertical(g32)
    c: Coincident(g33,g32)
    c: Horizontal(g33)
    c: Coincident(g34,g33)
    c: Vertical(g34)
    c: Block(g33)
    c: Coincident(g35,g13)
    c: Coincident(g35,g34)
    c: Horizontal(g35)
    c: Coincident(g36,g13)
    c: Coincident(g36,g20)
    c: Coincident(g37,g20)
    c: Coincident(g37,g30)
    c: Block(g30)
    c: Coincident(g38,g1)
    c: Coincident(g38,g2)
    c: Coincident(g39,g1)
    c: Coincident(g39,g2)
    c: Coincident(g40,g3)
    c: Coincident(g40,g4)
    c: Coincident(g41,g3)
    c: Coincident(g41,g4)
    c: Coincident(g42,g5)
    c: Coincident(g42,g6)
    c: Coincident(g43,g5)
    c: Coincident(g43,g6)
    c: Coincident(g44,g7)
    c: Coincident(g44,g8)
    c: Coincident(g45,g7)
    c: Coincident(g45,g8)
    c: Distance(g30) = 256
    c: Distance(g33) = 100
FEATURE [Part::Extrusion] Extrude002
  Base = -> Sketch001
  Dir = (1,0,0)
  DirMode = 2
  FaceMakerClass = Part::FaceMakerBullseye
  LengthFwd = 8
  LengthRev = 0
  Solid = true
  Symmetric = false
FEATURE [Sketcher::SketchObject] Sketch002
  FullyConstrained = true
  sketch-geometry (20):
    g0: LineSegment StartX=-2.77179 StartY=-200.304 StartZ=0 EndX=5.22821 EndY=-200.304 EndZ=0
    g1: LineSegment StartX=5.22821 StartY=-200.304 StartZ=0 EndX=5.22821 EndY=-197.304 EndZ=0
    g2: LineSegment StartX=-2.77179 StartY=-200.304 StartZ=0 EndX=-2.77179 EndY=-197.304 EndZ=0
    g3: LineSegment StartX=5.22821 StartY=-197.304 StartZ=0 EndX=8.22821 EndY=-197.304 EndZ=0
    g4: LineSegment StartX=-2.77179 StartY=-197.304 StartZ=0 EndX=-5.77179 EndY=-197.304 EndZ=0
    g5: LineSegment StartX=19.2282 StartY=-203.304 StartZ=0 EndX=19.2282 EndY=-206.304 EndZ=0
    g6: LineSegment StartX=-16.7718 StartY=-203.304 StartZ=0 EndX=-16.7718 EndY=-206.304 EndZ=0
    g7: LineSegment StartX=-16.7718 StartY=-206.304 StartZ=0 EndX=19.2282 EndY=-206.304 EndZ=0
    g8: Circle CenterX=-16.7718 CenterY=-203.304 CenterZ=0 NormalX=0 NormalY=0 NormalZ=1 AngleXU=0 Radius=1
    g9: Circle CenterX=-5.77179 CenterY=-203.304 CenterZ=0 NormalX=0 NormalY=0 NormalZ=1 AngleXU=0 Radius=1
    g10: Circle CenterX=-5.77179 CenterY=-197.304 CenterZ=0 NormalX=0 NormalY=0 NormalZ=1 AngleXU=0 Radius=1
    g11: BSplineCurve PolesCount=3 KnotsCount=2 Degree=2 IsPeriodic=0
    g12: GeomPoint X=-16.7718 Y=-203.304 Z=0
    g13: GeomPoint X=-5.77179 Y=-197.304 Z=0
    g14: Circle CenterX=19.2282 CenterY=-203.304 CenterZ=0 NormalX=0 NormalY=0 NormalZ=1 AngleXU=0 Radius=1
    g15: Circle CenterX=8.22821 CenterY=-203.304 CenterZ=0 NormalX=0 NormalY=0 NormalZ=1 AngleXU=0 Radius=1
    g16: Circle CenterX=8.22821 CenterY=-197.304 CenterZ=0 NormalX=0 NormalY=0 NormalZ=1 AngleXU=0 Radius=1
    g17: BSplineCurve PolesCount=3 KnotsCount=2 Degree=2 IsPeriodic=0
    g18: GeomPoint X=19.2282 Y=-203.304 Z=0
    g19: GeomPoint X=8.22821 Y=-197.304 Z=0
  constraints (41):
    c: Horizontal(g0)
    c: Distance(g0) = 8
    c: Coincident(g1,g0)
    c: Vertical(g1)
    c: Distance(g1) = 3
    c: Coincident(g2,g0)
    c: Vertical(g2)
    c: Distance(g2) = 3
    c: Coincident(g3,g1)
    c: Horizontal(g3)
    c: Distance(g3) = 3
    c: Coincident(g4,g2)
    c: Horizontal(g4)
    c: Distance(g4) = 3
    c: Vertical(g5)
    c: Vertical(g6)
    c: Coincident(g7,g6)
    c: Coincident(g7,g5)
    c: Weight(g8) = 1
    c: Equal(g8,g9)
    c: Equal(g8,g10)
    c: Coincident(g11,g4)
    c: InternalAlignment(g8,g11)
    c: InternalAlignment(g9,g11)
    c: InternalAlignment(g10,g11)
    c: InternalAlignment(g12,g11)
    c: InternalAlignment(g13,g11)
    c: Coincident(g17,g5)
    c: Weight(g14) = 1
    c: Equal(g14,g15)
    c: Equal(g14,g16)
    c: Coincident(g17,g3)
    c: InternalAlignment(g14,g17)
    c: InternalAlignment(g15,g17)
    c: InternalAlignment(g16,g17)
    c: InternalAlignment(g18,g17)
    c: InternalAlignment(g19,g17)
    c: Block(g7)
    c: Block(g17)
    c: Block(g11)
    c: Block(g6)
FEATURE [Part::Extrusion] Extrude003
  Base = -> Sketch002
  Dir = (0,0,1)
  DirMode = 2
  FaceMakerClass = Part::FaceMakerBullseye
  LengthFwd = 260
  LengthRev = 0
  Solid = true
  Symmetric = false
FEATURE [Part::Extrusion] Extrude
  Base = -> Sketch
  Dir = (0,0,1)
  DirMode = 2
  FaceMakerClass = Part::FaceMakerBullseye
  LengthFwd = 14
  LengthRev = 0
  Solid = true
  Symmetric = false
